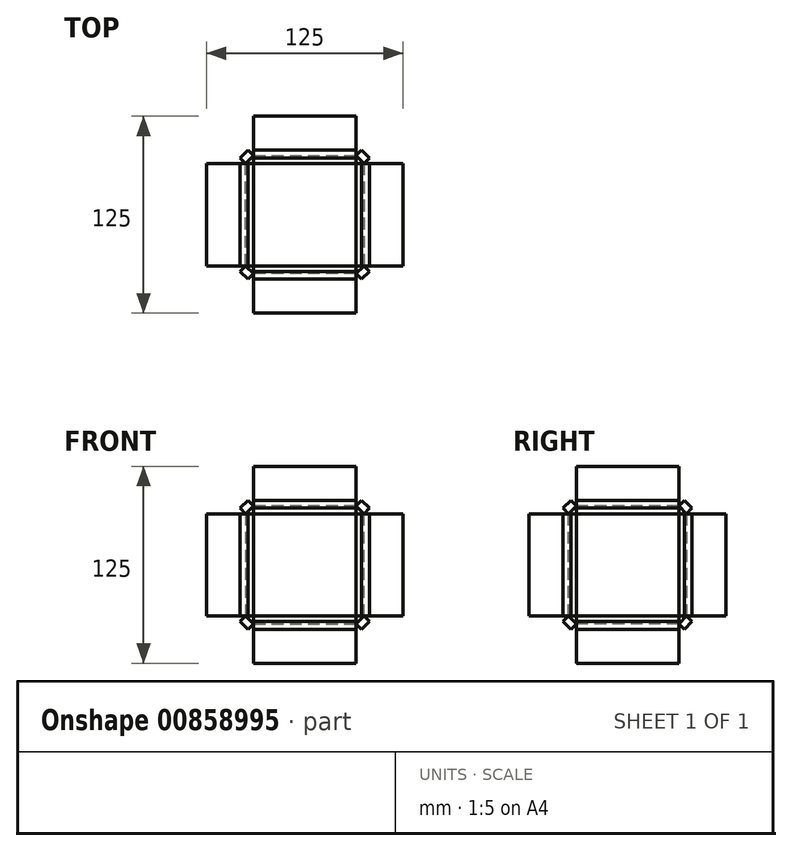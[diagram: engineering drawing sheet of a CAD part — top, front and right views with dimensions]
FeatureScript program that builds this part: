
annotation { "Feature Type Name" : "Feature", "Feature Type Description" : "" }
export const myFeature = defineFeature(function(context is Context, id is Id, definition is map)
    precondition{}
    {
        {
            var Q0;
            Q0=qCreatedBy(makeId("Top.planeOp"),FACE);
            var sketch = newSketch(context, id + "F0", { "sketchPlane" : qUnion([Q0])});
            skLineSegment(sketch, "E0.bottom", {"start": v(0, 0) * mm, "end": v(-75, 0) * mm});
            skLineSegment(sketch, "E0.top", {"start": v(0, 75) * mm, "end": v(-75, 75) * mm});
            skLineSegment(sketch, "E0.left", {"start": v(0, 0) * mm, "end": v(0, 75) * mm});
            skLineSegment(sketch, "E0.right", {"start": v(-75, 0) * mm, "end": v(-75, 75) * mm});
            skSolve(sketch);
        }
        {
            var Q0;
            Q0 = qSketchRegion(id + "F0", true);
            extrude(context, id + "F1", {"entities" : qUnion([Q0]), "depth" : 75 * mm, "offsetDistance" : 25 * mm});
        }
        {
            var Q0;
            Q0=makeQuery(id+"F1.opExtrude","CAP_EDGE",EDGE,{"disambiguationData":[OSD([sQuery(id+"F0.wireOp",EDGE,"E0.right")])],"isStart":false});
            var Q1;
            Q1=makeQuery(id+"F1.opExtrude","CAP_EDGE",EDGE,{"disambiguationData":[OSD([sQuery(id+"F0.wireOp",EDGE,"E0.bottom")])],"isStart":false});
            var Q2;
            Q2=makeQuery(id+"F1.opExtrude","CAP_EDGE",EDGE,{"disambiguationData":[OSD([sQuery(id+"F0.wireOp",EDGE,"E0.left")])],"isStart":false});
            var Q3;
            Q3=makeQuery(id+"F1.opExtrude","CAP_EDGE",EDGE,{"disambiguationData":[OSD([sQuery(id+"F0.wireOp",EDGE,"E0.top")])],"isStart":false});
            var Q4;
            Q4=makeQuery(id+"F1.opExtrude","SWEPT_EDGE",EDGE,{"disambiguationData":[OSD([sQuery(id+"F0.wireOp",EDGE,"E0.top"),sQuery(id+"F0.wireOp",EDGE,"E0.left")])]});
            var Q5;
            Q5=makeQuery(id+"F1.opExtrude","SWEPT_EDGE",EDGE,{"disambiguationData":[OSD([sQuery(id+"F0.wireOp",EDGE,"E0.top"),sQuery(id+"F0.wireOp",EDGE,"E0.right")])]});
            var Q6;
            Q6=makeQuery(id+"F1.opExtrude","CAP_EDGE",EDGE,{"disambiguationData":[OSD([sQuery(id+"F0.wireOp",EDGE,"E0.top")])],"isStart":true});
            var Q7;
            Q7=makeQuery(id+"F1.opExtrude","SWEPT_EDGE",EDGE,{"disambiguationData":[OSD([sQuery(id+"F0.wireOp",EDGE,"E0.bottom"),sQuery(id+"F0.wireOp",EDGE,"E0.right")])]});
            var Q8;
            Q8=makeQuery(id+"F1.opExtrude","CAP_EDGE",EDGE,{"disambiguationData":[OSD([sQuery(id+"F0.wireOp",EDGE,"E0.right")])],"isStart":true});
            var Q9;
            Q9=makeQuery(id+"F1.opExtrude","CAP_EDGE",EDGE,{"disambiguationData":[OSD([sQuery(id+"F0.wireOp",EDGE,"E0.left")])],"isStart":true});
            var Q10;
            Q10=makeQuery(id+"F1.opExtrude","SWEPT_EDGE",EDGE,{"disambiguationData":[OSD([sQuery(id+"F0.wireOp",EDGE,"E0.bottom"),sQuery(id+"F0.wireOp",EDGE,"E0.left")])]});
            var Q11;
            Q11=makeQuery(id+"F1.opExtrude","CAP_EDGE",EDGE,{"disambiguationData":[OSD([sQuery(id+"F0.wireOp",EDGE,"E0.bottom")])],"isStart":true});
            chamfer(context, id + "F2", {"entities" : qUnion([Q0, Q1, Q2, Q3, Q4, Q5, Q6, Q7, Q8, Q9, Q10, Q11]), "width" : 5 * mm, "tangentPropagation" : true});
        }
        {
            var Q0;
            {var subQ0=sQuery(id+"F0.wireOp",EDGE,"E0.right");Q0=makeQuery(id+"F2.opChamfer","BLEND_FACE",FACE,{"disambiguationData":[OSD([subQ0]),TDD([makeQuery(id+"F1.opExtrude","CAP_EDGE",EDGE,{"disambiguationData":[OSD([subQ0])],"isStart":false})])]});}
            extrude(context, id + "F3", {"entities" : qUnion([Q0]), "operationType" : NewBodyOperationType.ADD, "depth" : 5 * mm, "offsetDistance" : 25 * mm});
        }
        {
            var Q0;
            {var subQ0=sQuery(id+"F0.wireOp",EDGE,"E0.top");Q0=makeQuery(id+"F2.opChamfer","BLEND_FACE",FACE,{"disambiguationData":[OSD([subQ0]),TDD([makeQuery(id+"F1.opExtrude","CAP_EDGE",EDGE,{"disambiguationData":[OSD([subQ0])],"isStart":false})])]});}
            extrude(context, id + "F4", {"entities" : qUnion([Q0]), "operationType" : NewBodyOperationType.ADD, "depth" : 5 * mm, "offsetDistance" : 25 * mm});
        }
        {
            var Q0;
            {var subQ0=sQuery(id+"F0.wireOp",EDGE,"E0.left");Q0=makeQuery(id+"F2.opChamfer","BLEND_FACE",FACE,{"disambiguationData":[OSD([subQ0]),TDD([makeQuery(id+"F1.opExtrude","CAP_EDGE",EDGE,{"disambiguationData":[OSD([subQ0])],"isStart":false})])]});}
            extrude(context, id + "F5", {"entities" : qUnion([Q0]), "operationType" : NewBodyOperationType.ADD, "depth" : 5 * mm, "offsetDistance" : 25 * mm});
        }
        {
            var Q0;
            {var subQ0=sQuery(id+"F0.wireOp",EDGE,"E0.bottom");Q0=makeQuery(id+"F2.opChamfer","BLEND_FACE",FACE,{"disambiguationData":[OSD([subQ0]),TDD([makeQuery(id+"F1.opExtrude","CAP_EDGE",EDGE,{"disambiguationData":[OSD([subQ0])],"isStart":false})])]});}
            extrude(context, id + "F6", {"entities" : qUnion([Q0]), "operationType" : NewBodyOperationType.ADD, "depth" : 5 * mm, "offsetDistance" : 25 * mm});
        }
        {
            var Q0;
            {var subQ0=sQuery(id+"F0.wireOp",EDGE,"E0.left");var subQ1=sQuery(id+"F0.wireOp",EDGE,"E0.top");Q0=makeQuery(id+"F2.opChamfer","BLEND_FACE",FACE,{"disambiguationData":[OSD([subQ1,subQ0]),TDD([makeQuery(id+"F1.opExtrude","SWEPT_EDGE",EDGE,{"disambiguationData":[OSD([subQ1,subQ0])]})])]});}
            extrude(context, id + "F7", {"entities" : qUnion([Q0]), "operationType" : NewBodyOperationType.ADD, "depth" : 5 * mm, "offsetDistance" : 25 * mm});
        }
        {
            var Q0;
            {var subQ0=sQuery(id+"F0.wireOp",EDGE,"E0.left");Q0=makeQuery(id+"F2.opChamfer","BLEND_FACE",FACE,{"disambiguationData":[OSD([subQ0]),TDD([makeQuery(id+"F1.opExtrude","CAP_EDGE",EDGE,{"disambiguationData":[OSD([subQ0])],"isStart":true})])]});}
            extrude(context, id + "F8", {"entities" : qUnion([Q0]), "operationType" : NewBodyOperationType.ADD, "depth" : 5 * mm, "offsetDistance" : 25 * mm});
        }
        {
            var Q0;
            {var subQ0=sQuery(id+"F0.wireOp",EDGE,"E0.left");var subQ1=sQuery(id+"F0.wireOp",EDGE,"E0.bottom");Q0=makeQuery(id+"F2.opChamfer","BLEND_FACE",FACE,{"disambiguationData":[OSD([subQ1,subQ0]),TDD([makeQuery(id+"F1.opExtrude","SWEPT_EDGE",EDGE,{"disambiguationData":[OSD([subQ1,subQ0])]})])]});}
            extrude(context, id + "F9", {"entities" : qUnion([Q0]), "operationType" : NewBodyOperationType.ADD, "depth" : 5 * mm, "offsetDistance" : 25 * mm});
        }
        {
            var Q0;
            {var subQ0=sQuery(id+"F0.wireOp",EDGE,"E0.top");Q0=makeQuery(id+"F2.opChamfer","BLEND_FACE",FACE,{"disambiguationData":[OSD([subQ0]),TDD([makeQuery(id+"F1.opExtrude","CAP_EDGE",EDGE,{"disambiguationData":[OSD([subQ0])],"isStart":true})])]});}
            extrude(context, id + "F10", {"entities" : qUnion([Q0]), "operationType" : NewBodyOperationType.ADD, "depth" : 5 * mm, "offsetDistance" : 25 * mm});
        }
        {
            var Q0;
            {var subQ0=sQuery(id+"F0.wireOp",EDGE,"E0.bottom");Q0=makeQuery(id+"F2.opChamfer","BLEND_FACE",FACE,{"disambiguationData":[OSD([subQ0]),TDD([makeQuery(id+"F1.opExtrude","CAP_EDGE",EDGE,{"disambiguationData":[OSD([subQ0])],"isStart":true})])]});}
            extrude(context, id + "F11", {"entities" : qUnion([Q0]), "operationType" : NewBodyOperationType.ADD, "depth" : 5 * mm, "offsetDistance" : 25 * mm});
        }
        {
            var Q0;
            {var subQ0=sQuery(id+"F0.wireOp",EDGE,"E0.right");var subQ1=sQuery(id+"F0.wireOp",EDGE,"E0.top");Q0=makeQuery(id+"F2.opChamfer","BLEND_FACE",FACE,{"disambiguationData":[OSD([subQ1,subQ0]),TDD([makeQuery(id+"F1.opExtrude","SWEPT_EDGE",EDGE,{"disambiguationData":[OSD([subQ1,subQ0])]})])]});}
            extrude(context, id + "F12", {"entities" : qUnion([Q0]), "operationType" : NewBodyOperationType.ADD, "depth" : 5 * mm, "offsetDistance" : 25 * mm});
        }
        {
            var Q0;
            {var subQ0=sQuery(id+"F0.wireOp",EDGE,"E0.right");Q0=makeQuery(id+"F2.opChamfer","BLEND_FACE",FACE,{"disambiguationData":[OSD([subQ0]),TDD([makeQuery(id+"F1.opExtrude","CAP_EDGE",EDGE,{"disambiguationData":[OSD([subQ0])],"isStart":true})])]});}
            extrude(context, id + "F13", {"entities" : qUnion([Q0]), "operationType" : NewBodyOperationType.ADD, "depth" : 5 * mm, "offsetDistance" : 25 * mm});
        }
        {
            var Q0;
            {var subQ0=sQuery(id+"F0.wireOp",EDGE,"E0.right");var subQ1=sQuery(id+"F0.wireOp",EDGE,"E0.bottom");Q0=makeQuery(id+"F2.opChamfer","BLEND_FACE",FACE,{"disambiguationData":[OSD([subQ1,subQ0]),TDD([makeQuery(id+"F1.opExtrude","SWEPT_EDGE",EDGE,{"disambiguationData":[OSD([subQ1,subQ0])]})])]});}
            extrude(context, id + "F14", {"entities" : qUnion([Q0]), "operationType" : NewBodyOperationType.ADD, "depth" : 5 * mm, "offsetDistance" : 25 * mm});
        }
        {
            var Q0;
            Q0=makeQuery(id+"F1.opExtrude","SWEPT_FACE",FACE,{"disambiguationData":[OSD([sQuery(id+"F0.wireOp",EDGE,"E0.right")])]});
            extrude(context, id + "F15", {"entities" : qUnion([Q0]), "operationType" : NewBodyOperationType.ADD, "depth" : 25 * mm, "offsetDistance" : 25 * mm});
        }
        {
            var Q0;
            Q0=makeQuery(id+"F1.opExtrude","CAP_FACE",FACE,{"disambiguationData":[OSD([sQuery(id+"F0.wireOp",EDGE,"E0.bottom"),sQuery(id+"F0.wireOp",EDGE,"E0.top"),sQuery(id+"F0.wireOp",EDGE,"E0.left"),sQuery(id+"F0.wireOp",EDGE,"E0.right")])],"isStart":false});
            extrude(context, id + "F16", {"entities" : qUnion([Q0]), "operationType" : NewBodyOperationType.ADD, "depth" : 25 * mm, "offsetDistance" : 25 * mm});
        }
        {
            var Q0;
            Q0=makeQuery(id+"F1.opExtrude","SWEPT_FACE",FACE,{"disambiguationData":[OSD([sQuery(id+"F0.wireOp",EDGE,"E0.left")])]});
            extrude(context, id + "F17", {"entities" : qUnion([Q0]), "operationType" : NewBodyOperationType.ADD, "depth" : 25 * mm, "offsetDistance" : 25 * mm});
        }
        {
            var Q0;
            Q0=makeQuery(id+"F1.opExtrude","CAP_FACE",FACE,{"disambiguationData":[OSD([sQuery(id+"F0.wireOp",EDGE,"E0.bottom"),sQuery(id+"F0.wireOp",EDGE,"E0.top"),sQuery(id+"F0.wireOp",EDGE,"E0.left"),sQuery(id+"F0.wireOp",EDGE,"E0.right")])],"isStart":true});
            extrude(context, id + "F18", {"entities" : qUnion([Q0]), "operationType" : NewBodyOperationType.ADD, "depth" : 25 * mm, "offsetDistance" : 25 * mm});
        }
        {
            var Q0;
            Q0=makeQuery(id+"F1.opExtrude","SWEPT_FACE",FACE,{"disambiguationData":[OSD([sQuery(id+"F0.wireOp",EDGE,"E0.bottom")])]});
            extrude(context, id + "F19", {"entities" : qUnion([Q0]), "operationType" : NewBodyOperationType.ADD, "depth" : 25 * mm, "offsetDistance" : 25 * mm});
        }
        {
            var Q0;
            Q0=makeQuery(id+"F1.opExtrude","SWEPT_FACE",FACE,{"disambiguationData":[OSD([sQuery(id+"F0.wireOp",EDGE,"E0.top")])]});
            extrude(context, id + "F20", {"entities" : qUnion([Q0]), "operationType" : NewBodyOperationType.ADD, "depth" : 25 * mm, "offsetDistance" : 25 * mm});
        }
    });
